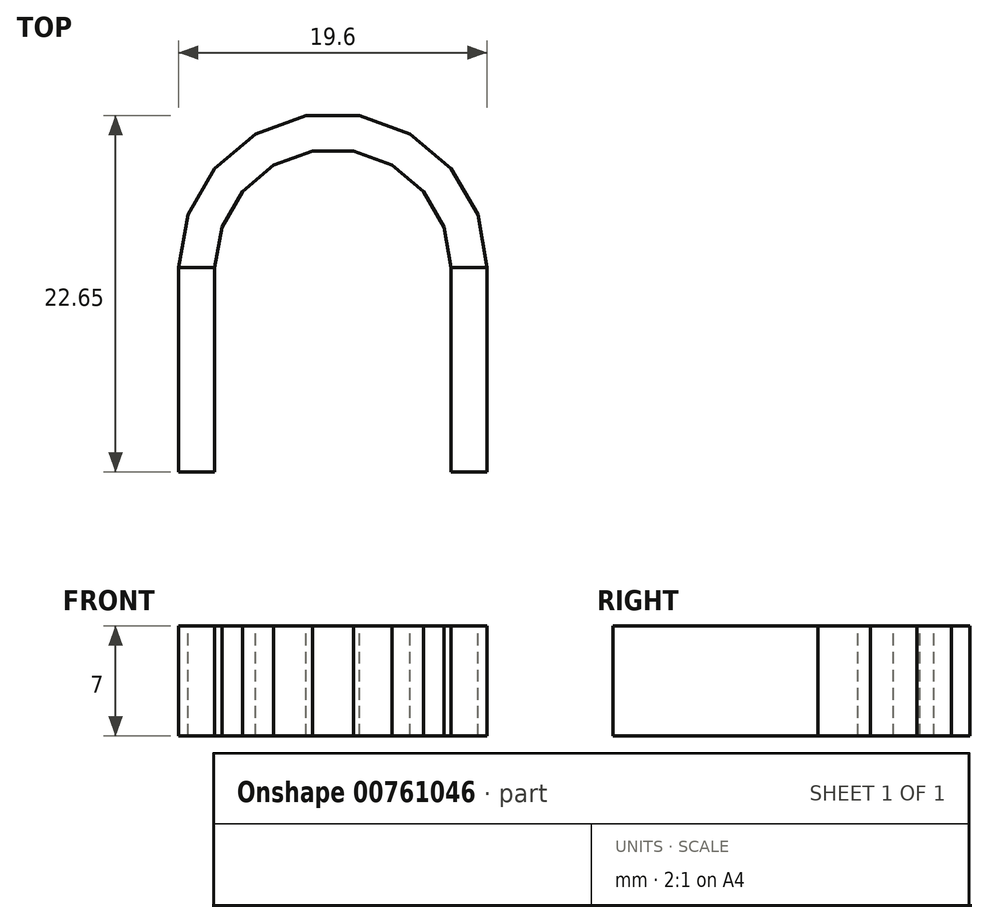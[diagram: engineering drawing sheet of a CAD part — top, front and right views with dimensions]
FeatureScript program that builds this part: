
annotation { "Feature Type Name" : "Feature", "Feature Type Description" : "" }
export const myFeature = defineFeature(function(context is Context, id is Id, definition is map)
    precondition{}
    {
        {
            var Q0;
            Q0=qCreatedBy(makeId("Top.planeOp"),FACE);
            var sketch = newSketch(context, id + "F0", { "sketchPlane" : qUnion([Q0])});
            skLineSegment(sketch, "E0", {"start": v(0, 0) * mm, "end": v(2.6, 0) * mm});
            skLineSegment(sketch, "E1", {"start": v(1.3, 0) * mm, "end": v(1.3, 2.3) * mm, "construction": true});
            skLineSegment(sketch, "E2", {"start": v(1.3, 2.3) * mm, "end": v(3, 2.3) * mm});
            skLineSegment(sketch, "E3", {"start": v(3, 2.3) * mm, "end": v(2.6, 0) * mm});
            skLineSegment(sketch, "E4", {"start": v(1.3, 2.3) * mm, "end": v(-0.4, 2.3) * mm});
            skLineSegment(sketch, "E5", {"start": v(-0.4, 2.3) * mm, "end": v(0, 0) * mm});
            skLineSegment(sketch, "E6.bottom", {"start": v(-0.4, 2.3) * mm, "end": v(3, 2.3) * mm});
            skLineSegment(sketch, "E6.top", {"start": v(-0.4, 7.3) * mm, "end": v(3, 7.3) * mm});
            skLineSegment(sketch, "E6.left", {"start": v(-0.4, 2.3) * mm, "end": v(-0.4, 7.3) * mm});
            skLineSegment(sketch, "E6.right", {"start": v(3, 2.3) * mm, "end": v(3, 7.3) * mm});
            skLineSegment(sketch, "E7.MirrorCS", {"start": v(-0.4, 7.3) * mm, "end": v(0, 9.6) * mm});
            skLineSegment(sketch, "E8.MirrorCS", {"start": v(3, 7.3) * mm, "end": v(2.6, 9.6) * mm});
            skLineSegment(sketch, "E9.MirrorCS", {"start": v(0, 9.6) * mm, "end": v(2.6, 9.6) * mm});
            skLineSegment(sketch, "E10", {"start": v(0, 0) * mm, "end": v(0, -5) * mm});
            skLineSegment(sketch, "E11", {"start": v(0, -5) * mm, "end": v(2.6, -5) * mm});
            skLineSegment(sketch, "E12", {"start": v(2.6, -5) * mm, "end": v(2.6, 0) * mm});
            skLineSegment(sketch, "E13", {"start": v(2.6, 0) * mm, "end": v(0, 0) * mm});
            skLineSegment(sketch, "E14.bottom", {"start": v(3, 7.3) * mm, "end": v(5.3, 7.3) * mm});
            skLineSegment(sketch, "E14.top", {"start": v(3, 2.3) * mm, "end": v(5.3, 2.3) * mm});
            skLineSegment(sketch, "E14.left", {"start": v(3, 7.3) * mm, "end": v(3, 2.3) * mm});
            skLineSegment(sketch, "E14.right", {"start": v(5.3, 7.3) * mm, "end": v(5.3, 2.3) * mm});
            skLineSegment(sketch, "E15.MirrorCS", {"start": v(-0.4, 2.3) * mm, "end": v(-2.7, 2.3) * mm});
            skLineSegment(sketch, "E16.MirrorCS", {"start": v(-2.7, 7.3) * mm, "end": v(-2.7, 2.3) * mm});
            skLineSegment(sketch, "E17.MirrorCS", {"start": v(-0.4, 7.3) * mm, "end": v(-2.7, 7.3) * mm});
            skSolve(sketch);
        }
        {
            var Q0;
            Q0=qCreatedBy(makeId("Top.planeOp"),FACE);
            var sketch = newSketch(context, id + "F1", { "sketchPlane" : qUnion([Q0])});
            skCircle(sketch, "E18", {"center": v(0, 0) * mm, "radius": 7.5 * mm, "construction": true});
            skLineSegment(sketch, "E19.1.0", {"start": v(0, 0) * mm, "end": v(3.32, 18.84) * mm, "construction": true});
            skLineSegment(sketch, "E19.3.0", {"start": v(0, 0) * mm, "end": v(9.57, 16.57) * mm, "construction": true});
            skLineSegment(sketch, "E19.5.0", {"start": v(0, 0) * mm, "end": v(14.66, 12.3) * mm, "construction": true});
            skLineSegment(sketch, "E19.7.0", {"start": v(0, 0) * mm, "end": v(17.98, 6.54) * mm, "construction": true});
            skLineSegment(sketch, "E19.9.0", {"start": v(0, 0) * mm, "end": v(19.13, 0) * mm, "construction": true});
            skLineSegment(sketch, "E19.anchor2", {"start": v(0, 0) * mm, "end": v(19.13, 0) * mm, "construction": true});
            skLineSegment(sketch, "E20.MirrorCS", {"start": v(0, 0) * mm, "end": v(-19.13, 0) * mm, "construction": true});
            skLineSegment(sketch, "E21.MirrorCS", {"start": v(0, 0) * mm, "end": v(-17.98, 6.54) * mm, "construction": true});
            skLineSegment(sketch, "E22.MirrorCS", {"start": v(0, 0) * mm, "end": v(-14.66, 12.3) * mm, "construction": true});
            skLineSegment(sketch, "E23.MirrorCS", {"start": v(0, 0) * mm, "end": v(-3.32, 18.84) * mm, "construction": true});
            skLineSegment(sketch, "E24.MirrorCS", {"start": v(0, 0) * mm, "end": v(-9.57, 16.57) * mm, "construction": true});
            skLineSegment(sketch, "E25", {"start": v(-7.5, 0) * mm, "end": v(-7.05, 2.57) * mm});
            skLineSegment(sketch, "E26", {"start": v(-7.05, 2.57) * mm, "end": v(-5.75, 4.82) * mm});
            skLineSegment(sketch, "E27", {"start": v(-5.75, 4.82) * mm, "end": v(-3.75, 6.5) * mm});
            skLineSegment(sketch, "E28", {"start": v(-3.75, 6.5) * mm, "end": v(-1.3, 7.39) * mm});
            skLineSegment(sketch, "E29", {"start": v(-1.3, 7.39) * mm, "end": v(1.3, 7.39) * mm});
            skLineSegment(sketch, "E30", {"start": v(1.3, 7.39) * mm, "end": v(3.75, 6.5) * mm});
            skLineSegment(sketch, "E31", {"start": v(3.75, 6.5) * mm, "end": v(5.75, 4.82) * mm});
            skLineSegment(sketch, "E32", {"start": v(5.75, 4.82) * mm, "end": v(7.05, 2.57) * mm});
            skLineSegment(sketch, "E33", {"start": v(7.05, 2.57) * mm, "end": v(7.5, 0) * mm});
            skCircle(sketch, "E34.0", {"center": v(0, 0) * mm, "radius": 9.8 * mm, "construction": true});
            skLineSegment(sketch, "E35", {"start": v(-9.8, 0) * mm, "end": v(-9.2, 3.35) * mm});
            skLineSegment(sketch, "E36", {"start": v(-9.2, 3.35) * mm, "end": v(-7.5, 6.3) * mm});
            skLineSegment(sketch, "E37", {"start": v(-7.5, 6.3) * mm, "end": v(-4.9, 8.49) * mm});
            skLineSegment(sketch, "E38", {"start": v(-4.9, 8.49) * mm, "end": v(-1.7, 9.65) * mm});
            skLineSegment(sketch, "E39", {"start": v(-1.7, 9.65) * mm, "end": v(1.7, 9.65) * mm});
            skLineSegment(sketch, "E40", {"start": v(1.7, 9.65) * mm, "end": v(4.9, 8.49) * mm});
            skLineSegment(sketch, "E41", {"start": v(4.9, 8.49) * mm, "end": v(7.5, 6.3) * mm});
            skLineSegment(sketch, "E42", {"start": v(7.5, 6.3) * mm, "end": v(9.2, 3.35) * mm});
            skLineSegment(sketch, "E43", {"start": v(9.2, 3.35) * mm, "end": v(9.8, 0) * mm});
            skLineSegment(sketch, "E44", {"start": v(-9.8, 0) * mm, "end": v(-7.5, 0) * mm});
            skLineSegment(sketch, "E45", {"start": v(-9.2, 3.35) * mm, "end": v(-7.05, 2.57) * mm});
            skLineSegment(sketch, "E46", {"start": v(-7.5, 6.3) * mm, "end": v(-5.75, 4.82) * mm});
            skLineSegment(sketch, "E47", {"start": v(-4.9, 8.49) * mm, "end": v(-3.75, 6.5) * mm});
            skLineSegment(sketch, "E48", {"start": v(-1.7, 9.65) * mm, "end": v(-1.3, 7.39) * mm});
            skLineSegment(sketch, "E49", {"start": v(1.7, 9.65) * mm, "end": v(1.3, 7.39) * mm});
            skLineSegment(sketch, "E50", {"start": v(4.9, 8.49) * mm, "end": v(3.75, 6.5) * mm});
            skLineSegment(sketch, "E51", {"start": v(7.5, 6.3) * mm, "end": v(5.75, 4.82) * mm});
            skLineSegment(sketch, "E52", {"start": v(9.2, 3.35) * mm, "end": v(7.05, 2.57) * mm});
            skLineSegment(sketch, "E53", {"start": v(9.8, 0) * mm, "end": v(7.5, 0) * mm});
            skLineSegment(sketch, "E54", {"start": v(-9.8, 0) * mm, "end": v(-9.8, -13) * mm});
            skLineSegment(sketch, "E55", {"start": v(-7.5, 0) * mm, "end": v(-7.5, -13) * mm});
            skLineSegment(sketch, "E56", {"start": v(-7.5, -13) * mm, "end": v(-9.8, -13) * mm});
            skLineSegment(sketch, "E57.MirrorCS", {"start": v(7.5, 0) * mm, "end": v(7.5, -13) * mm});
            skLineSegment(sketch, "E58.MirrorCS", {"start": v(9.8, 0) * mm, "end": v(9.8, -13) * mm});
            skLineSegment(sketch, "E59.MirrorCS", {"start": v(7.5, -13) * mm, "end": v(9.8, -13) * mm});
            skSolve(sketch);
        }
        {
            var Q0;
            Q0=makeQuery(id+"F1.imprint","IMPRINT",FACE,{"disambiguationData":[TD([[makeQuery(id+"F1.imprint","IMPRINT",EDGE,{"derivedFrom":sQuery(id+"F1.wireOp",EDGE,"E33")}),1.0]])]});
            var Q1;
            Q1=makeQuery(id+"F1.imprint","IMPRINT",FACE,{"disambiguationData":[TD([[makeQuery(id+"F1.imprint","IMPRINT",EDGE,{"derivedFrom":sQuery(id+"F1.wireOp",EDGE,"E32")}),1.0]])]});
            var Q2;
            Q2=makeQuery(id+"F1.imprint","IMPRINT",FACE,{"disambiguationData":[TD([[makeQuery(id+"F1.imprint","IMPRINT",EDGE,{"derivedFrom":sQuery(id+"F1.wireOp",EDGE,"E31")}),1.0]])]});
            var Q3;
            Q3=makeQuery(id+"F1.imprint","IMPRINT",FACE,{"disambiguationData":[TD([[makeQuery(id+"F1.imprint","IMPRINT",EDGE,{"derivedFrom":sQuery(id+"F1.wireOp",EDGE,"E30")}),1.0]])]});
            var Q4;
            Q4=makeQuery(id+"F1.imprint","IMPRINT",FACE,{"disambiguationData":[TD([[makeQuery(id+"F1.imprint","IMPRINT",EDGE,{"derivedFrom":sQuery(id+"F1.wireOp",EDGE,"E29")}),1.0]])]});
            var Q5;
            Q5=makeQuery(id+"F1.imprint","IMPRINT",FACE,{"disambiguationData":[TD([[makeQuery(id+"F1.imprint","IMPRINT",EDGE,{"derivedFrom":sQuery(id+"F1.wireOp",EDGE,"E28")}),1.0]])]});
            var Q6;
            Q6=makeQuery(id+"F1.imprint","IMPRINT",FACE,{"disambiguationData":[TD([[makeQuery(id+"F1.imprint","IMPRINT",EDGE,{"derivedFrom":sQuery(id+"F1.wireOp",EDGE,"E27")}),1.0]])]});
            var Q7;
            Q7=makeQuery(id+"F1.imprint","IMPRINT",FACE,{"disambiguationData":[TD([[makeQuery(id+"F1.imprint","IMPRINT",EDGE,{"derivedFrom":sQuery(id+"F1.wireOp",EDGE,"E26")}),1.0]])]});
            var Q8;
            Q8=makeQuery(id+"F1.imprint","IMPRINT",FACE,{"disambiguationData":[TD([[makeQuery(id+"F1.imprint","IMPRINT",EDGE,{"derivedFrom":sQuery(id+"F1.wireOp",EDGE,"E25")}),1.0]])]});
            extrude(context, id + "F2", {"entities" : qUnion([Q0, Q1, Q2, Q3, Q4, Q5, Q6, Q7, Q8]), "oppositeDirection" : true, "depth" : 7 * mm, "offsetDistance" : 25 * mm});
        }
        {
            var Q0;
            Q0=makeQuery(id+"F1.imprint","IMPRINT",FACE,{"disambiguationData":[TD([[makeQuery(id+"F1.imprint","IMPRINT",EDGE,{"derivedFrom":sQuery(id+"F1.wireOp",EDGE,"E44")}),-1.0]])]});
            var Q1;
            Q1=makeQuery(id+"F1.imprint","IMPRINT",FACE,{"disambiguationData":[TD([[makeQuery(id+"F1.imprint","IMPRINT",EDGE,{"derivedFrom":sQuery(id+"F1.wireOp",EDGE,"E53")}),1.0]])]});
            extrude(context, id + "F3", {"entities" : qUnion([Q0, Q1]), "oppositeDirection" : true, "depth" : 7 * mm, "offsetDistance" : 25 * mm, "hasSecondDirection" : true, "secondDirectionOppositeDirection" : false, "secondDirectionDepth" : 0 * mm});
        }
    });
